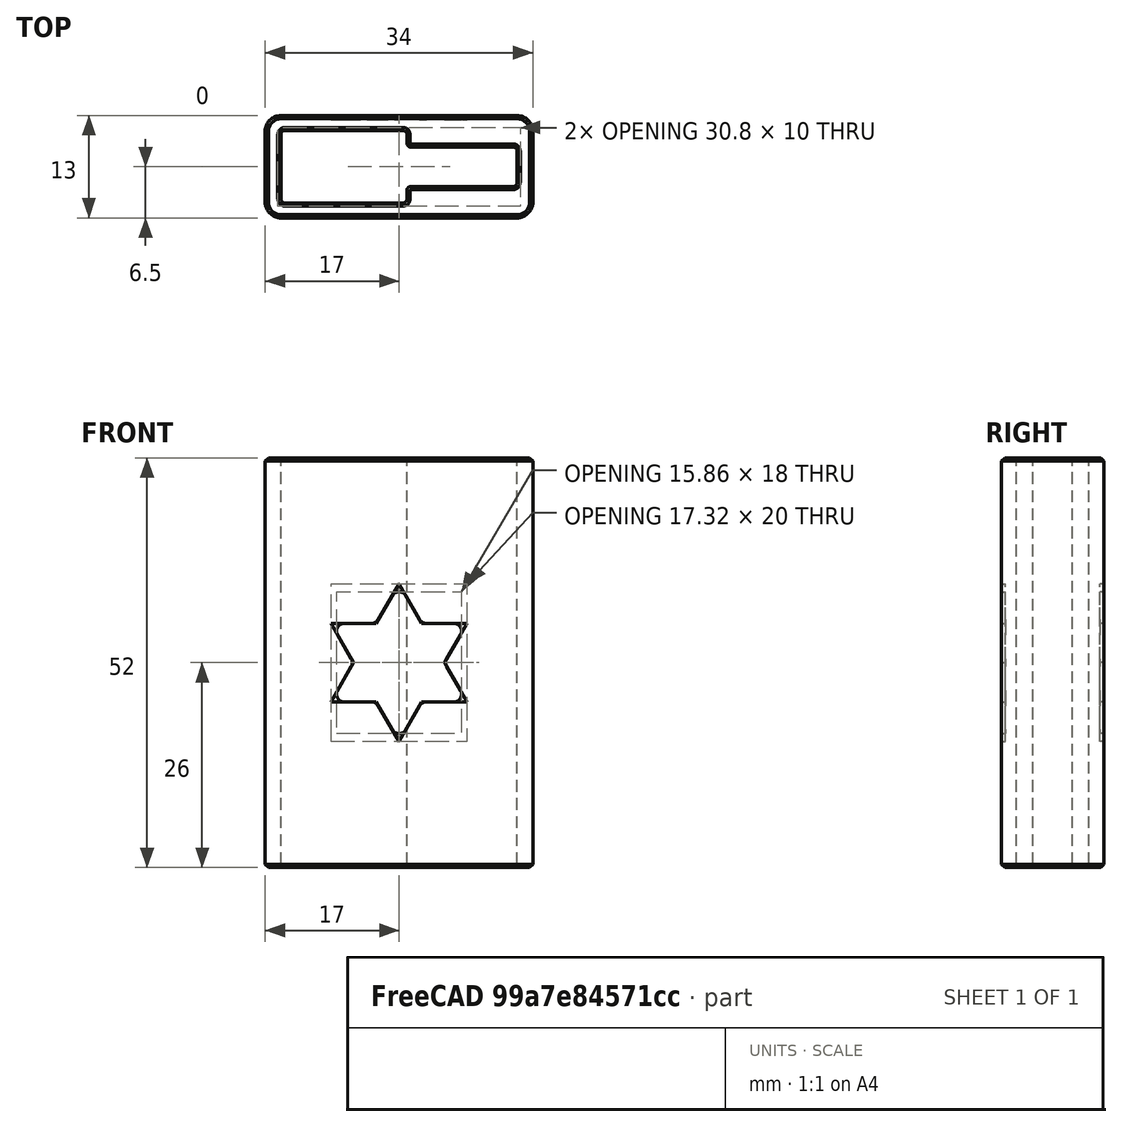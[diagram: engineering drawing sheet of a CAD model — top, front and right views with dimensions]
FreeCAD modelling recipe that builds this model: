
FCSTD DOCUMENT  (FreeCAD 0.17R13522 (Git))
Label: lidl_taco_puntas_torx
License: All rights reserved
LicenseURL: http://en.wikipedia.org/wiki/All_rights_reserved
objects: Part::Box×3, Part::Fillet×3, Mesh::Feature×1, Part::Fuse×1, Part::Cut×1, Part::Chamfer×1, PartDesign::FeatureBase×1, Sketcher::SketchObject×1, PartDesign::Pocket×1, PartDesign::Mirrored×1, PartDesign::Body×1
note: 15 computed .brp shape members not serialized (recipe doc carries the construction recipe); baked Part::Feature solids carry a one-line shape summary decoded from their .brp

FEATURE [Mesh::Feature] lidl
FEATURE [Part::Box] Box  label="Cubo"
  AttacherType = Attacher::AttachEngine3D
  Height = 60
  Length = 16
  Placement = pos=(0,-4.6,0) rot=(0,0,1;0rad)
  Width = 9.2
FEATURE [Part::Box] Box001  label="Cubo001"
  AttacherType = Attacher::AttachEngine3D
  Height = 60
  Length = 30
  Placement = pos=(0,-2.5,0) rot=(0,0,1;0rad)
  Width = 5
FEATURE [Part::Fuse] Fusion
  Base = -> Box
  Refine = true
  Tool = -> Box001
FEATURE [Part::Fillet] Fillet
  Base = -> Fusion
  Edges = 8 edges r=0.5: [Edge2,Edge4,Edge6,Edge9,Edge12,Edge16,Edge18,Edge20]
FEATURE [Part::Box] Box002  label="Cubo002"
  AttacherType = Attacher::AttachEngine3D
  Height = 52
  Length = 34
  Placement = pos=(-2,-6.5,0) rot=(0,0,1;0rad)
  Width = 13
FEATURE [Part::Cut] Cut
  Base = -> Box002
  Refine = true
  Tool = -> Fillet
FEATURE [Part::Fillet] Fillet001
  Base = -> Cut
  Edges = 4 edges r=2: [Edge1,Edge3,Edge6,Edge27]
FEATURE [Part::Chamfer] Chamfer
  Base = -> Fillet001
  Edges = 48 edges r=0.4: [Edge1,Edge4,Edge5,Edge6,Edge7,Edge8,Edge9,Edge10,Edge11,Edge12,Edge13,Edge14,Edge15,Edge16,Edge17,Edge18,Edge19,Edge20,Edge21,Edge22,Edge23,Edge24,Edge25,Edge26,Edge27,Edge28,Edge30,Edge32,Edge33,Edge34,Edge35,Edge36,Edge37,Edge38,Edge39,Edge40,Edge41,Edge42,Edge43,Edge44,Edge45,Edge46,Edge47,+5 more]
FEATURE [PartDesign::FeatureBase] BaseFeature
  BaseFeature = -> Chamfer
FEATURE [Sketcher::SketchObject] Sketch
  MapMode = 5
  Placement = pos=(0,-6.5,0) rot=(1,0,0;1.5708rad)
  Support = -> [BaseFeature]
  sketch-geometry (19):
    g0: LineSegment [constr] StartX=15 StartY=36 StartZ=0 EndX=6.33975 EndY=31 EndZ=0
    g1: LineSegment [constr] StartX=6.33975 StartY=31 StartZ=0 EndX=6.33975 EndY=21 EndZ=0
    g2: LineSegment [constr] StartX=6.33975 StartY=21 StartZ=0 EndX=15 EndY=16 EndZ=0
    g3: LineSegment [constr] StartX=15 StartY=16 StartZ=0 EndX=23.6603 EndY=21 EndZ=0
    g4: LineSegment [constr] StartX=23.6603 StartY=21 StartZ=0 EndX=23.6603 EndY=31 EndZ=0
    g5: LineSegment [constr] StartX=23.6603 StartY=31 StartZ=0 EndX=15 EndY=36 EndZ=0
    g6: Circle [constr] CenterX=15 CenterY=26 CenterZ=0 NormalX=0 NormalY=0 NormalZ=1 AngleXU=0 Radius=10
    g7: LineSegment StartX=15 StartY=36 StartZ=0 EndX=12.1132 EndY=31 EndZ=0
    g8: LineSegment StartX=6.33975 StartY=21 StartZ=0 EndX=12.1132 EndY=21 EndZ=0
    g9: LineSegment StartX=23.6603 StartY=21 StartZ=0 EndX=20.7735 EndY=26 EndZ=0
    g10: LineSegment StartX=6.33975 StartY=31 StartZ=0 EndX=9.2265 EndY=26 EndZ=0
    g11: LineSegment StartX=15 StartY=16 StartZ=0 EndX=17.8868 EndY=21 EndZ=0
    g12: LineSegment StartX=23.6603 StartY=31 StartZ=0 EndX=17.8868 EndY=31 EndZ=0
    g13: LineSegment StartX=9.2265 StartY=26 StartZ=0 EndX=6.33975 EndY=21 EndZ=0
    g14: LineSegment StartX=12.1132 StartY=31 StartZ=0 EndX=6.33975 EndY=31 EndZ=0
    g15: LineSegment StartX=17.8868 StartY=31 StartZ=0 EndX=15 EndY=36 EndZ=0
    g16: LineSegment StartX=20.7735 StartY=26 StartZ=0 EndX=23.6603 EndY=31 EndZ=0
    g17: LineSegment StartX=17.8868 StartY=21 StartZ=0 EndX=23.6603 EndY=21 EndZ=0
    g18: LineSegment StartX=12.1132 StartY=21 StartZ=0 EndX=15 EndY=16 EndZ=0
  constraints (41):
    c: Coincident(g0,g1)
    c: Coincident(g1,g2)
    c: Coincident(g2,g3)
    c: Coincident(g3,g4)
    c: Coincident(g4,g5)
    c: Coincident(g5,g0)
    c: Equal(g0, g1-g5) x5
    c: PointOnObject(g0,g6)
    c: PointOnObject(g1,g6)
    c: PointOnObject(g2,g6)
    c: PointOnObject(g3,g6)
    c: PointOnObject(g4,g6)
    c: PointOnObject(g5,g6)
    c: Coincident(g0,g7)
    c: Coincident(g13,g1)
    c: Coincident(g13,g8)
    c: Coincident(g17,g9)
    c: Coincident(g15,g7)
    c: Coincident(g17,g3)
    c: Vertical(g4)
    c: DistanceX(g-1,g6) = 15
    c: DistanceY(g-1,g6) = 26
    c: Radius(g6) = 10
    c: Coincident(g0,g10)
    c: Coincident(g18,g2)
    c: Coincident(g18,g11)
    c: Coincident(g16,g12)
    c: Coincident(g14,g10)
    c: Coincident(g16,g4)
    c: Tangent(g7,g13)
    c: Coincident(g14,g7)
    c: Tangent(g12,g14)
    c: Coincident(g15,g12)
    c: Tangent(g9,g15)
    c: Coincident(g16,g9)
    c: Tangent(g11,g16)
    c: Coincident(g17,g11)
    c: Tangent(g8,g17)
    c: Coincident(g10,g13)
    c: Coincident(g18,g8)
    c: Tangent(g10,g18)
FEATURE [PartDesign::Pocket] Pocket
  BaseFeature = -> BaseFeature
  Length = 0.5
  Length2 = 100
  Profile = -> Sketch
  Refine = true
  Type = 0
FEATURE [PartDesign::Mirrored] Mirrored
  BaseFeature = -> Pocket
  MirrorPlane = -> XZ_Plane
  Originals = -> [Pocket]
  Refine = true
FEATURE [PartDesign::Body] Body
  BaseFeature = -> Chamfer
  Group = -> [BaseFeature,Sketch,Pocket,Mirrored]
  Origin = -> Origin
  Tip = -> Mirrored
FEATURE [Part::Fillet] Fillet002
  Base = -> Mirrored
  Edges = 24 edges r=1: [Edge102,Edge104,Edge105,Edge107,Edge109,Edge111,Edge113,Edge115,Edge117,Edge119,Edge121,Edge123,Edge201,Edge203,Edge204,Edge206,Edge208,Edge210,Edge212,Edge214,Edge216,Edge218,Edge220,Edge222]
